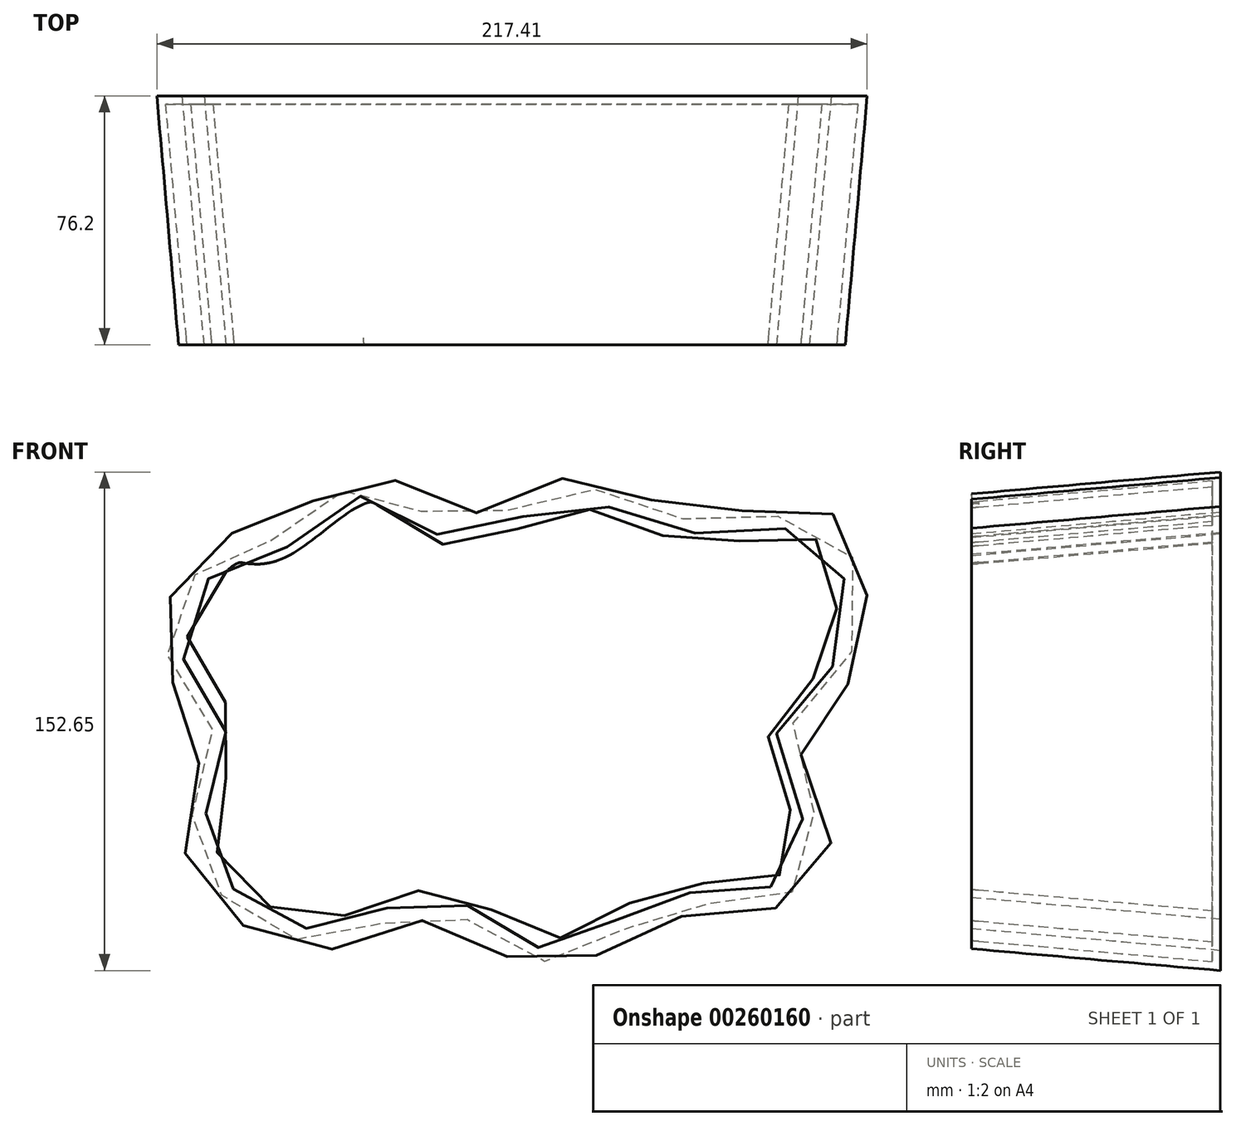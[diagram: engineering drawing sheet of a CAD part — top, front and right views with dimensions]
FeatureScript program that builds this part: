
annotation { "Feature Type Name" : "Feature", "Feature Type Description" : "" }
export const myFeature = defineFeature(function(context is Context, id is Id, definition is map)
    precondition{}
    {
        {
            var Q0;
            Q0=qCreatedBy(makeId("Front.planeOp"),FACE);
            var sketch = newSketch(context, id + "F0", { "sketchPlane" : qUnion([Q0])});
            skFitSpline(sketch, "E0", {"points": [v(-102.75, 78.94) * mm, v(-71.33, 97.36) * mm, v(-46.56, 84.07) * mm, v(-11.22, 95.55) * mm, v(28.35, 85.28) * mm, v(73.36, 82.26) * mm, v(74.27, 31.5) * mm, v(59.77, 17.3) * mm, v(69.74, -18.34) * mm, v(52.82, -36.16) * mm, v(19.6, -39.78) * mm, v(-19.07, -55.2) * mm, v(-49.89, -39.78) * mm, v(-89.46, -49.15) * mm, v(-128.73, -15.92) * mm, v(-122.39, 18.82) * mm, v(-136.58, 43.6) * mm, v(-115.44, 78.03) * mm, v(-102.75, 78.94) * mm]});
            skSolve(sketch);
        }
        {
            var Q0;
            Q0=makeQuery(id+"F0.imprint","IMPRINT",FACE,{"disambiguationData":[TD([[makeQuery(id+"F0.imprint","IMPRINT",EDGE,{"derivedFrom":sQuery(id+"F0.wireOp",EDGE,"E0")}),-1.0]])]});
            extrude(context, id + "F1", {"entities" : qUnion([Q0]), "depth" : 76.2 * mm, "hasDraft" : true, "draftAngle" : 5 * degree, "draftPullDirection" : true});
        }
        {
            var Q0;
            Q0=makeQuery(id+"F1.opExtrude","CAP_FACE",FACE,{"disambiguationData":[OSD([sQuery(id+"F0.wireOp",EDGE,"E0")])],"isStart":false});
            shell(context, id + "F2", {"entities" : qUnion([Q0]), "thickness" : 2.54 * mm});
        }
    });
